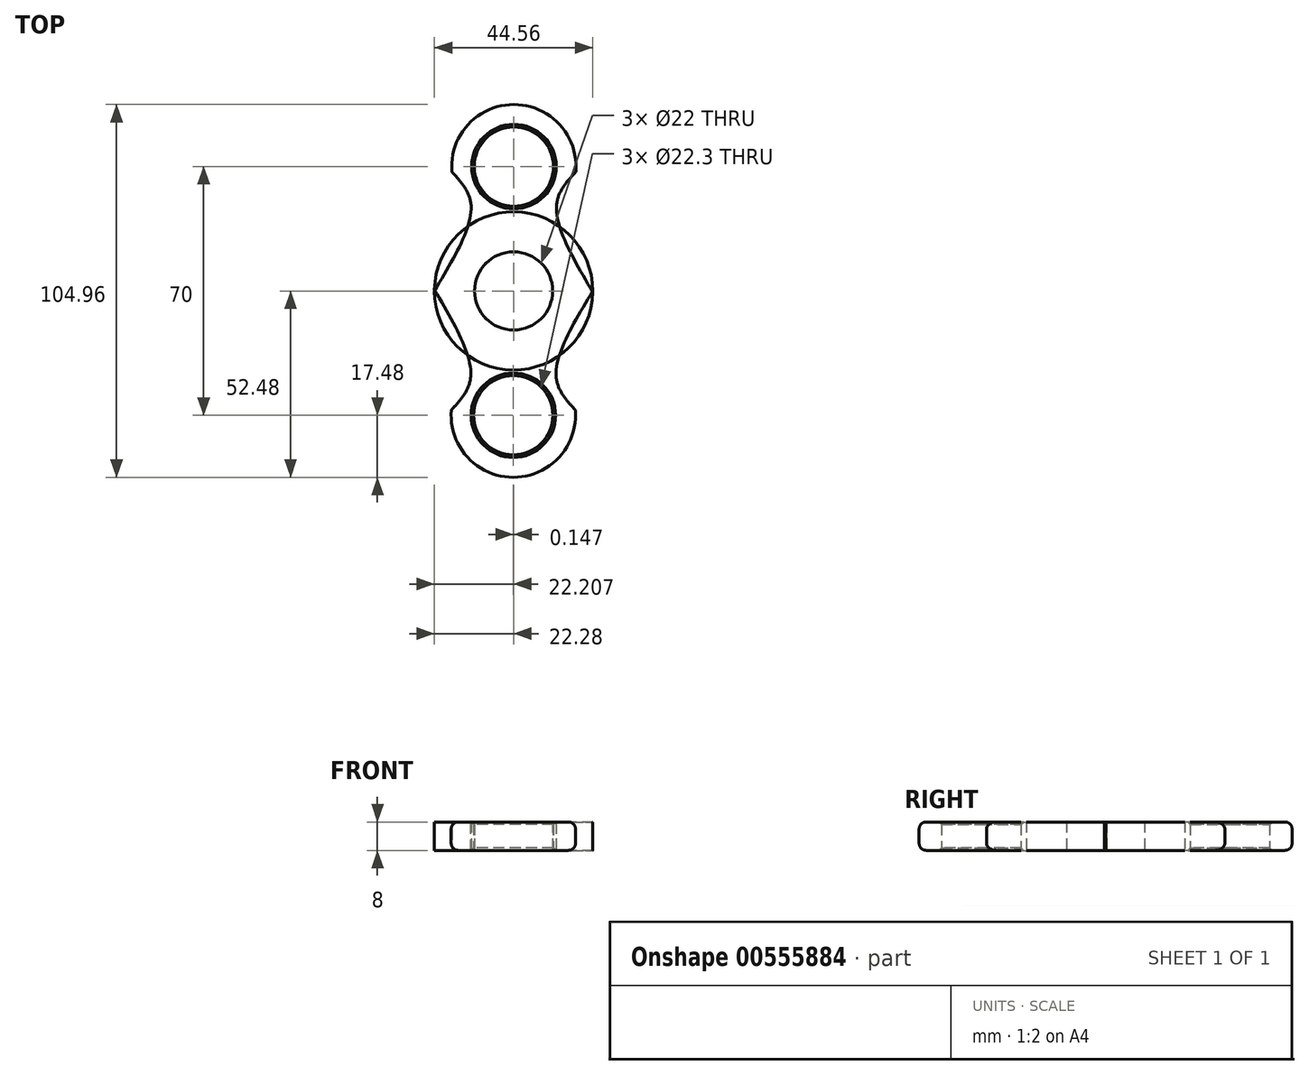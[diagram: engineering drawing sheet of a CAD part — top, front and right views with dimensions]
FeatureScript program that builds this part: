
annotation { "Feature Type Name" : "Feature", "Feature Type Description" : "" }
export const myFeature = defineFeature(function(context is Context, id is Id, definition is map)
    precondition{}
    {
        {
            var Q0;
            Q0=qCreatedBy(makeId("Top.planeOp"),FACE);
            var sketch = newSketch(context, id + "F0", { "sketchPlane" : qUnion([Q0])});
            skCircle(sketch, "E0.MirrorC", {"center": v(0, 0) * mm, "radius": 11 * mm});
            skCircle(sketch, "E1", {"center": v(-0.07, -35) * mm, "radius": 11.15 * mm});
            skArc(sketch, "E2", {"start": v(22.28, 0) * mm, "mid": v(0.16, 22.28) * mm, "end": v(-22.27, 0.33) * mm});
            skArc(sketch, "E3", {"start": v(-17.51, -33.53) * mm, "mid": v(-0.07, -52.48) * mm, "end": v(17.36, -33.53) * mm});
            skLineSegment(sketch, "E4", {"start": v(-0.07, -34.98) * mm, "end": v(0, 0) * mm});
            skLineSegment(sketch, "E5", {"start": v(-0.05, -23.85) * mm, "end": v(-12.05, -23.82) * mm});
            skLineSegment(sketch, "E6", {"start": v(-0.05, -23.85) * mm, "end": v(11.95, -23.84) * mm});
            skFitSpline(sketch, "E7", {"points": [v(17.36, -33.53) * mm, v(11.95, -23.84) * mm, v(22.28, 0) * mm], "startDerivative": vector(-19.78, 21.56) * mm, "endDerivative": vector(26.38, 43.93) * mm});
            skFitSpline(sketch, "E8", {"points": [v(-17.51, -33.53) * mm, v(-12.05, -23.82) * mm, v(-22.27, 0.33) * mm], "startDerivative": vector(19.9, 21.57) * mm, "endDerivative": vector(-26.19, 44.52) * mm});
            skSolve(sketch);
        }
        {
            var Q0;
            Q0 = qSketchRegion(id + "F0", true);
            extrude(context, id + "F1", {"entities" : qUnion([Q0]), "depth" : 8 * mm, "offsetDistance" : 25 * mm});
        }
        {
            var Q0;
            Q0=qCreatedBy(makeId("Front.planeOp"),FACE);
            var sketch = newSketch(context, id + "F2", { "sketchPlane" : qUnion([Q0])});
            skLineSegment(sketch, "E9", {"start": v(0, 0) * mm, "end": v(0, 31.73) * mm});
            skSolve(sketch);
        }
        {
            var Q0;
            Q0=makeQuery(id+"F1.opExtrude","SWEPT_BODY",BODY,{"disambiguationData":[OSD([sQuery(id+"F0.wireOp",EDGE,"b1288798-2a29-44ef-96ac-a017ccb4ea65"),sQuery(id+"F0.wireOp",EDGE,"E0.MirrorC"),sQuery(id+"F0.wireOp",EDGE,"E1"),sQuery(id+"F0.wireOp",EDGE,"c1382c52-a920-45b0-9801-b8ba2129e0ff"),sQuery(id+"F0.wireOp",EDGE,"f6ad5f9d-b599-4dff-a43c-700d636c7170"),sQuery(id+"F0.wireOp",EDGE,"Bgz7mtgj-ePqZ-xKAO-cXva-mmE5Scy1chzA")])]});
            var Q1;
            Q1=sQuery(id+"F2.wireOp",EDGE,"E9");
            circularPattern(context, id + "F3", {"entities" : qUnion([Q0]), "axis" : qUnion([Q1]), "angle" : 360 * degree, "instanceCount" : 2, "equalSpace" : true});
        }
        {
            var Q0;
            Q0=makeQuery(id+"F1.opExtrude","CAP_EDGE",EDGE,{"disambiguationData":[OSD([sQuery(id+"F0.wireOp",EDGE,"E1")])],"isStart":false});
            var Q1;
            Q1=makeQuery(id+"F1.opExtrude","CAP_EDGE",EDGE,{"disambiguationData":[OSD([sQuery(id+"F0.wireOp",EDGE,"E0.MirrorC")])],"isStart":false});
            var Q2;
            Q2=makeQuery(id+"F3.opPattern","COPY",EDGE,{"derivedFrom":makeQuery(id+"F1.opExtrude","CAP_EDGE",EDGE,{"disambiguationData":[OSD([sQuery(id+"F0.wireOp",EDGE,"E1")])],"isStart":false}),"instanceName":"1"});
            var Q3;
            Q3=makeQuery(id+"F3.opPattern","COPY",EDGE,{"derivedFrom":makeQuery(id+"F1.opExtrude","CAP_EDGE",EDGE,{"disambiguationData":[OSD([sQuery(id+"F0.wireOp",EDGE,"E0.MirrorC")])],"isStart":true}),"instanceName":"1"});
            var Q4;
            Q4=makeQuery(id+"F3.opPattern","COPY",EDGE,{"derivedFrom":makeQuery(id+"F1.opExtrude","CAP_EDGE",EDGE,{"disambiguationData":[OSD([sQuery(id+"F0.wireOp",EDGE,"E1")])],"isStart":true}),"instanceName":"1"});
            var Q5;
            Q5=makeQuery(id+"F1.opExtrude","CAP_EDGE",EDGE,{"disambiguationData":[OSD([sQuery(id+"F0.wireOp",EDGE,"E1")])],"isStart":true});
            var Q6;
            Q6=makeQuery(id+"F3.opPattern","COPY",EDGE,{"derivedFrom":makeQuery(id+"F1.opExtrude","CAP_EDGE",EDGE,{"disambiguationData":[OSD([sQuery(id+"F0.wireOp",EDGE,"E0.MirrorC")])],"isStart":false}),"instanceName":"1"});
            chamfer(context, id + "F4", {"entities" : qUnion([Q0, Q1, Q2, Q3, Q4, Q5, Q6]), "width" : 0.75 * mm, "tangentPropagation" : true});
        }
        {
            var Q0;
            Q0=makeQuery(id+"F1.opExtrude","SWEPT_BODY",BODY,{"disambiguationData":[OSD([sQuery(id+"F0.wireOp",EDGE,"b1288798-2a29-44ef-96ac-a017ccb4ea65"),sQuery(id+"F0.wireOp",EDGE,"E0.MirrorC"),sQuery(id+"F0.wireOp",EDGE,"E1"),sQuery(id+"F0.wireOp",EDGE,"3df68af3-a4c5-428b-8664-f6e59a6c0c3c"),sQuery(id+"F0.wireOp",EDGE,"a7de7a01-8356-4df7-8f22-34ebeca18d6d"),sQuery(id+"F0.wireOp",EDGE,"E2")])]});
            transform(context, id + "F5", {"entities" : qUnion([Q0]), "transformType" : TransformType.TRANSLATION_3D, "dx" : 0 * mm, "dy" : 0 * mm, "dz" : 0 * mm, "makeCopy" : true});
        }
        {
            var Q0;
            Q0=makeQuery(id+"F5.opPattern","COPY",EDGE,{"derivedFrom":makeQuery(id+"F1.opExtrude","CAP_EDGE",EDGE,{"disambiguationData":[OSD([sQuery(id+"F0.wireOp",EDGE,"E3")])],"isStart":true}),"instanceName":"1"});
            var Q1;
            Q1=makeQuery(id+"F5.opPattern","COPY",EDGE,{"derivedFrom":makeQuery(id+"F1.opExtrude","CAP_EDGE",EDGE,{"disambiguationData":[OSD([sQuery(id+"F0.wireOp",EDGE,"E3")])],"isStart":false}),"instanceName":"1"});
            var Q2;
            Q2=makeQuery(id+"F5.opPattern","COPY",EDGE,{"derivedFrom":makeQuery(id+"F1.opExtrude","CAP_EDGE",EDGE,{"disambiguationData":[OSD([sQuery(id+"F0.wireOp",EDGE,"a7de7a01-8356-4df7-8f22-34ebeca18d6d")])],"isStart":false}),"instanceName":"1"});
            var Q3;
            Q3=makeQuery(id+"F5.opPattern","COPY",EDGE,{"derivedFrom":makeQuery(id+"F1.opExtrude","CAP_EDGE",EDGE,{"disambiguationData":[OSD([sQuery(id+"F0.wireOp",EDGE,"a7de7a01-8356-4df7-8f22-34ebeca18d6d")])],"isStart":true}),"instanceName":"1"});
            var Q4;
            Q4=makeQuery(id+"F5.opPattern","COPY",EDGE,{"derivedFrom":makeQuery(id+"F1.opExtrude","CAP_EDGE",EDGE,{"disambiguationData":[OSD([sQuery(id+"F0.wireOp",EDGE,"3df68af3-a4c5-428b-8664-f6e59a6c0c3c")])],"isStart":true}),"instanceName":"1"});
            var Q5;
            Q5=makeQuery(id+"F5.opPattern","COPY",EDGE,{"derivedFrom":makeQuery(id+"F1.opExtrude","CAP_EDGE",EDGE,{"disambiguationData":[OSD([sQuery(id+"F0.wireOp",EDGE,"3df68af3-a4c5-428b-8664-f6e59a6c0c3c")])],"isStart":false}),"instanceName":"1"});
            fillet(context, id + "F6", {"entities" : qUnion([Q0, Q1, Q2, Q3, Q4, Q5]), "radius" : 2 * mm, "tangentPropagation" : true, "allowEdgeOverflow" : false});
        }
        {
            var Q0;
            Q0=makeQuery(id+"F1.opExtrude","CAP_EDGE",EDGE,{"disambiguationData":[OSD([sQuery(id+"F0.wireOp",EDGE,"3df68af3-a4c5-428b-8664-f6e59a6c0c3c")])],"isStart":false});
            var Q1;
            Q1=makeQuery(id+"F1.opExtrude","CAP_EDGE",EDGE,{"disambiguationData":[OSD([sQuery(id+"F0.wireOp",EDGE,"E3")])],"isStart":false});
            var Q2;
            Q2=makeQuery(id+"F1.opExtrude","CAP_EDGE",EDGE,{"disambiguationData":[OSD([sQuery(id+"F0.wireOp",EDGE,"3df68af3-a4c5-428b-8664-f6e59a6c0c3c")])],"isStart":true});
            var Q3;
            Q3=makeQuery(id+"F1.opExtrude","CAP_EDGE",EDGE,{"disambiguationData":[OSD([sQuery(id+"F0.wireOp",EDGE,"E3")])],"isStart":true});
            var Q4;
            Q4=makeQuery(id+"F1.opExtrude","CAP_EDGE",EDGE,{"disambiguationData":[OSD([sQuery(id+"F0.wireOp",EDGE,"a7de7a01-8356-4df7-8f22-34ebeca18d6d")])],"isStart":false});
            var Q5;
            Q5=makeQuery(id+"F1.opExtrude","CAP_EDGE",EDGE,{"disambiguationData":[OSD([sQuery(id+"F0.wireOp",EDGE,"a7de7a01-8356-4df7-8f22-34ebeca18d6d")])],"isStart":true});
            fillet(context, id + "F7", {"entities" : qUnion([Q0, Q1, Q2, Q3, Q4, Q5]), "radius" : 2 * mm, "tangentPropagation" : true, "allowEdgeOverflow" : false});
        }
        {
            var Q0;
            Q0=makeQuery(id+"F3.opPattern","COPY",EDGE,{"derivedFrom":makeQuery(id+"F1.opExtrude","CAP_EDGE",EDGE,{"disambiguationData":[OSD([sQuery(id+"F0.wireOp",EDGE,"a7de7a01-8356-4df7-8f22-34ebeca18d6d")])],"isStart":false}),"instanceName":"1"});
            var Q1;
            Q1=makeQuery(id+"F3.opPattern","COPY",EDGE,{"derivedFrom":makeQuery(id+"F1.opExtrude","CAP_EDGE",EDGE,{"disambiguationData":[OSD([sQuery(id+"F0.wireOp",EDGE,"a7de7a01-8356-4df7-8f22-34ebeca18d6d")])],"isStart":true}),"instanceName":"1"});
            var Q2;
            Q2=makeQuery(id+"F3.opPattern","COPY",EDGE,{"derivedFrom":makeQuery(id+"F1.opExtrude","CAP_EDGE",EDGE,{"disambiguationData":[OSD([sQuery(id+"F0.wireOp",EDGE,"E3")])],"isStart":false}),"instanceName":"1"});
            var Q3;
            Q3=makeQuery(id+"F3.opPattern","COPY",EDGE,{"derivedFrom":makeQuery(id+"F1.opExtrude","CAP_EDGE",EDGE,{"disambiguationData":[OSD([sQuery(id+"F0.wireOp",EDGE,"E3")])],"isStart":true}),"instanceName":"1"});
            var Q4;
            Q4=makeQuery(id+"F3.opPattern","COPY",EDGE,{"derivedFrom":makeQuery(id+"F1.opExtrude","CAP_EDGE",EDGE,{"disambiguationData":[OSD([sQuery(id+"F0.wireOp",EDGE,"3df68af3-a4c5-428b-8664-f6e59a6c0c3c")])],"isStart":false}),"instanceName":"1"});
            var Q5;
            Q5=makeQuery(id+"F3.opPattern","COPY",EDGE,{"derivedFrom":makeQuery(id+"F1.opExtrude","CAP_EDGE",EDGE,{"disambiguationData":[OSD([sQuery(id+"F0.wireOp",EDGE,"3df68af3-a4c5-428b-8664-f6e59a6c0c3c")])],"isStart":true}),"instanceName":"1"});
            fillet(context, id + "F8", {"entities" : qUnion([Q0, Q1, Q2, Q3, Q4, Q5]), "radius" : 2 * mm, "tangentPropagation" : true, "allowEdgeOverflow" : false});
        }
    });
